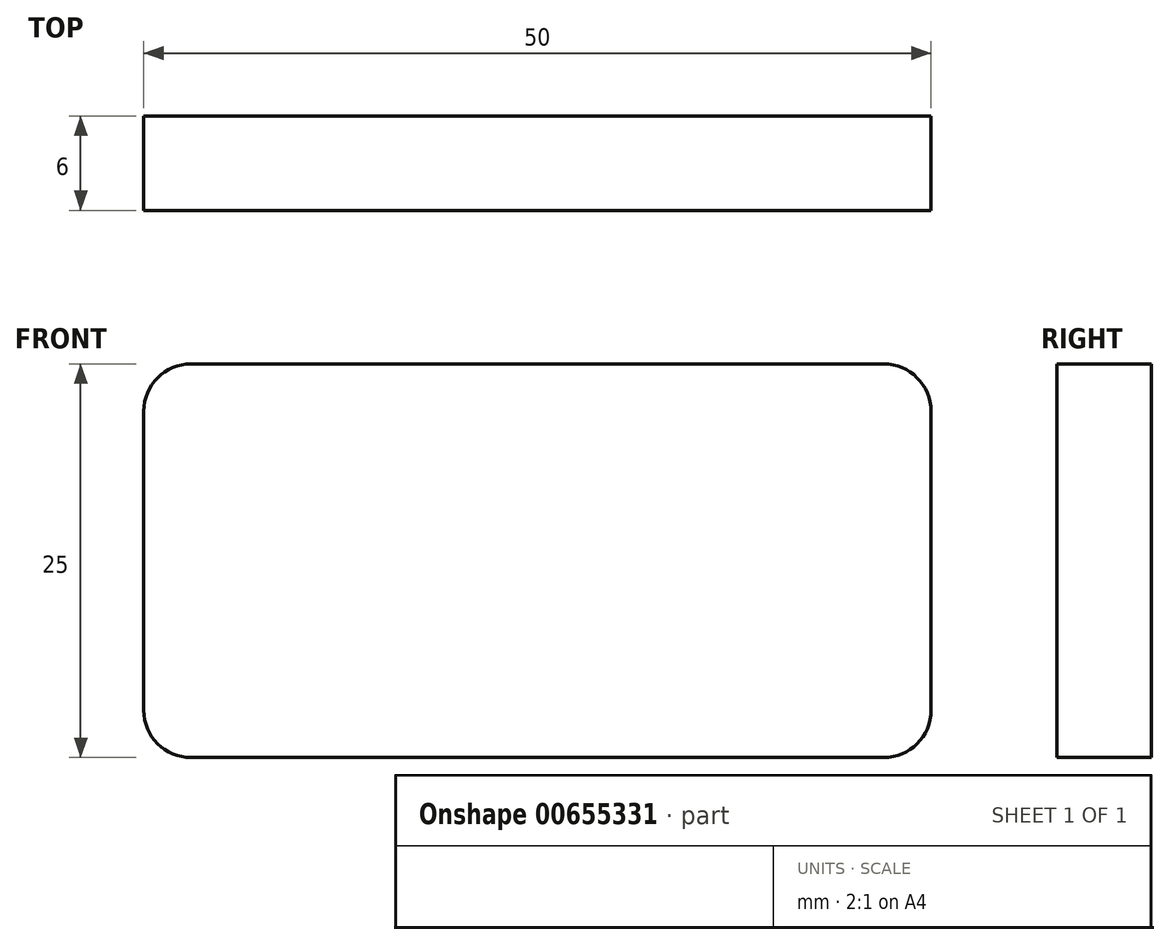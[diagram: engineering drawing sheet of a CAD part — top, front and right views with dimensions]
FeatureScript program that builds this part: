
annotation { "Feature Type Name" : "Feature", "Feature Type Description" : "" }
export const myFeature = defineFeature(function(context is Context, id is Id, definition is map)
    precondition{}
    {
        {
            var Q0;
            Q0=qCreatedBy(makeId("Front.planeOp"),FACE);
            var sketch = newSketch(context, id + "F0", { "sketchPlane" : qUnion([Q0])});
            skLineSegment(sketch, "E0.bottom", {"start": v(22, -12.5) * mm, "end": v(-22, -12.5) * mm});
            skLineSegment(sketch, "E0.top", {"start": v(22, 12.5) * mm, "end": v(-22, 12.5) * mm});
            skLineSegment(sketch, "E0.left", {"start": v(25, -9.5) * mm, "end": v(25, 9.5) * mm});
            skLineSegment(sketch, "E0.right", {"start": v(-25, -9.5) * mm, "end": v(-25, 9.5) * mm});
            skPoint(sketch, "E0.middle", {"position": v(0, 0) * mm});
            skPoint(sketch, "E1.visualSharp", {"position": v(-25, 12.5) * mm});
            skArc(sketch, "E1.filletArc", {"start": v(-22, 12.5) * mm, "mid": v(-24.12, 11.62) * mm, "end": v(-25, 9.5) * mm});
            skPoint(sketch, "E2.visualSharp", {"position": v(-25, -12.5) * mm});
            skArc(sketch, "E2.filletArc", {"start": v(-25, -9.5) * mm, "mid": v(-24.12, -11.62) * mm, "end": v(-22, -12.5) * mm});
            skPoint(sketch, "E3.visualSharp", {"position": v(25, -12.5) * mm});
            skArc(sketch, "E3.filletArc", {"start": v(22, -12.5) * mm, "mid": v(24.12, -11.62) * mm, "end": v(25, -9.5) * mm});
            skPoint(sketch, "E4.visualSharp", {"position": v(25, 12.5) * mm});
            skArc(sketch, "E4.filletArc", {"start": v(25, 9.5) * mm, "mid": v(24.12, 11.62) * mm, "end": v(22, 12.5) * mm});
            skSolve(sketch);
        }
        {
            var Q0;
            Q0=makeQuery(id+"F0.imprint","IMPRINT",FACE,{"disambiguationData":[TD([[makeQuery(id+"F0.imprint","IMPRINT",EDGE,{"derivedFrom":sQuery(id+"F0.wireOp",EDGE,"E0.bottom")}),-1.0]])]});
            extrude(context, id + "F1", {"entities" : qUnion([Q0]), "endBound" : BoundingType.SYMMETRIC, "depth" : 6 * mm, "offsetDistance" : 25 * mm});
        }
    });
